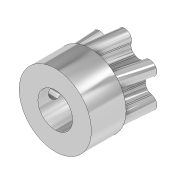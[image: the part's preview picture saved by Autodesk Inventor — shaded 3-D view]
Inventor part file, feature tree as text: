
AUTODESK INVENTOR PART (.ipt)
format: ipt  version: 2020 (Build 240168000, 168)  size: 363,008 bytes
history: native  units: in
note: dims shown in document units (in); Inventor stores cm internally (conversion verified against a paired STEP export)
features: sketch x5, extrude x2, sweep x1, other x1, projected_geometry x1
ambient origin geometry x8: Origin, YZ Plane, XZ Plane, XY Plane, X Axis, Y Axis, Z Axis, Center Point
bodies: Solid1 (feature_tree)
feature tree (10):
  sweep  "Sweep1"
  sketch  "3D Sketch2"
  extrude  "Extrusion1"  Depth=0.0787in
  extrude  "Extrusion2"  Depth=0.1969in
  sketch  "Sketch1"  dims[d0=0.1969in d1=0.4094in]
  sketch  "3D Sketch1"
  other  "Helical Curve1"
  sketch  "Sketch2"  dims[d2=0.0866in d3=0.0787in]
  projected_geometry  "Projected Loop1"
  sketch  "Sketch3"  dims[d4=0.0787in d5=0.0787in d6=2.3622in d8=360.0deg d10=0.1969in d11=0.0118in d12=0.236in d13=0.0in d14=0.0in d15=0.0in d16=0.1969in d17=0.0in d18=0.0787in d19=0.205in d20=0.0in]
